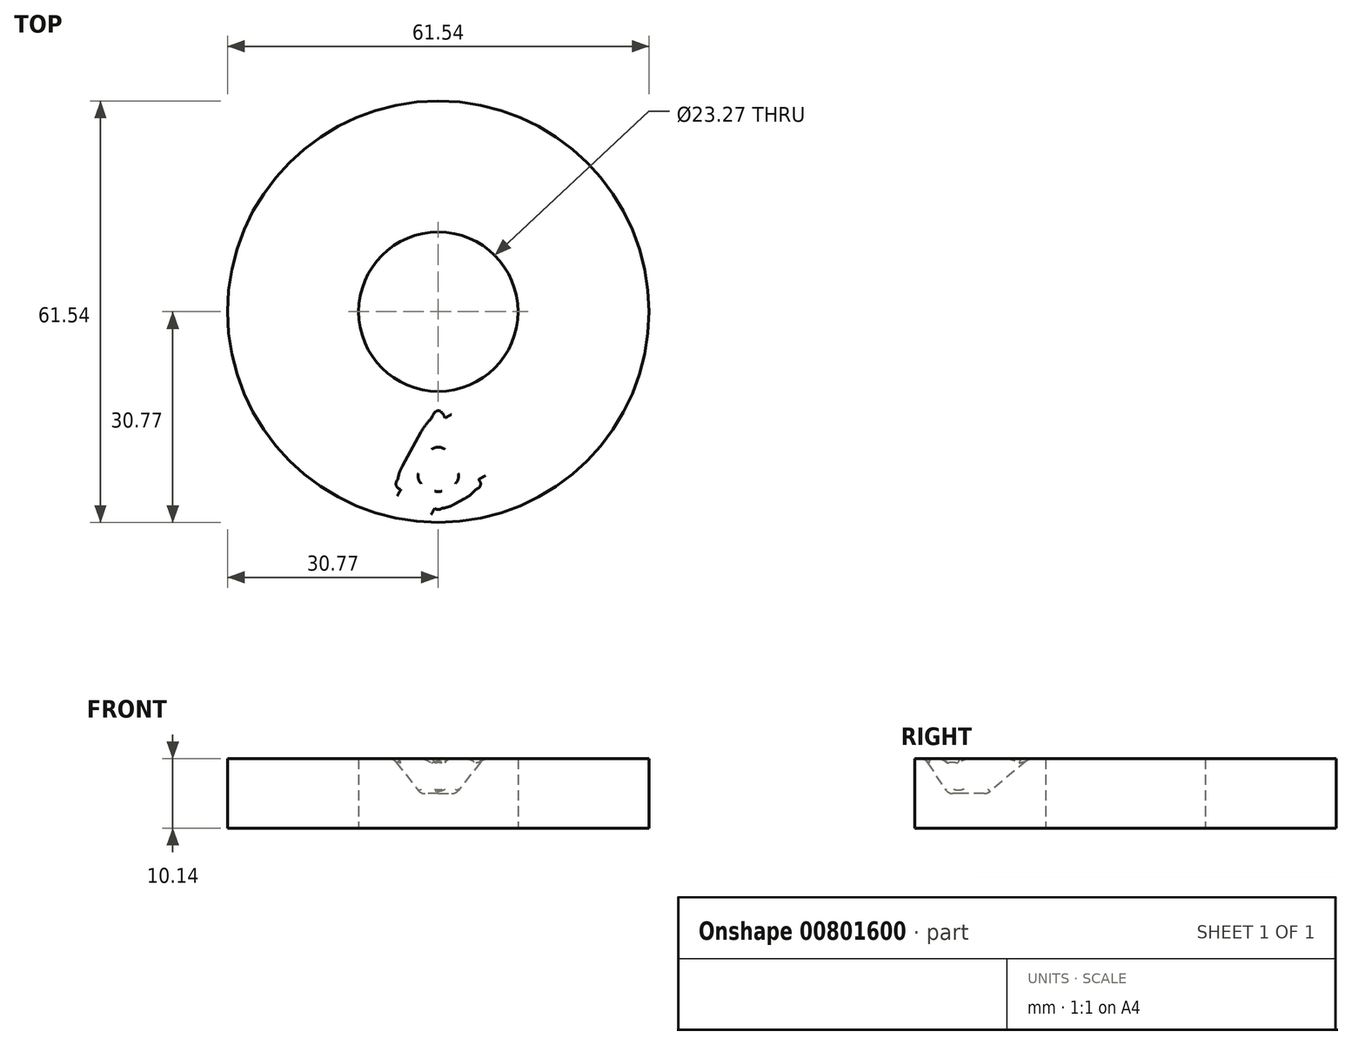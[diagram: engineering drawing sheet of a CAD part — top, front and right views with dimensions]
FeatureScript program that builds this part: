
annotation { "Feature Type Name" : "Feature", "Feature Type Description" : "" }
export const myFeature = defineFeature(function(context is Context, id is Id, definition is map)
    precondition{}
    {
        {
            var Q0;
            Q0=qCreatedBy(makeId("Top.planeOp"),FACE);
            var sketch = newSketch(context, id + "F0", { "sketchPlane" : qUnion([Q0])});
            skCircle(sketch, "E0", {"center": v(0, 0) * mm, "radius": 30.77 * mm});
            skCircle(sketch, "E1", {"center": v(0, 0) * mm, "radius": 11.63 * mm});
            skSolve(sketch);
        }
        {
            var Q0;
            Q0 = qSketchRegion(id + "F0", true);
            extrude(context, id + "F1", {"entities" : qUnion([Q0]), "depth" : 10.14 * mm, "offsetDistance" : 25.4 * mm});
        }
        {
            var Q0;
            Q0=makeQuery(id+"F1.opExtrude","CAP_FACE",FACE,{"disambiguationData":[OSD([sQuery(id+"F0.wireOp",EDGE,"E0"),sQuery(id+"F0.wireOp",EDGE,"E1")])],"isStart":false});
            var sketch = newSketch(context, id + "F2", { "sketchPlane" : qUnion([Q0])});
            skLineSegment(sketch, "E2", {"start": v(24.9, -25.58) * mm, "end": v(0, -13.03) * mm});
            skLineSegment(sketch, "E3", {"start": v(0, -13.03) * mm, "end": v(6.94, -25.58) * mm});
            skLineSegment(sketch, "E4", {"start": v(6.94, -25.58) * mm, "end": v(0, -29.4) * mm});
            skLineSegment(sketch, "E5.MirrorCS", {"start": v(0, -13.03) * mm, "end": v(-6.94, -25.58) * mm});
            skLineSegment(sketch, "E6.MirrorCS", {"start": v(-6.94, -25.58) * mm, "end": v(0, -29.4) * mm});
            skSolve(sketch);
        }
        {
            var Q0;
            Q0=makeQuery(id+"F2.imprint","IMPRINT",FACE,{"disambiguationData":[TD([[makeQuery(id+"F2.imprint","IMPRINT",EDGE,{"derivedFrom":sQuery(id+"F2.wireOp",EDGE,"E3")}),-1.0]])]});
            var Q1;
            Q1 = qSketchRegion(id + "F2", true);
            extrude(context, id + "F3", {"entities" : qUnion([Q0, Q1]), "operationType" : NewBodyOperationType.REMOVE, "oppositeDirection" : true, "depth" : 5.08 * mm, "offsetDistance" : 25.4 * mm, "hasDraft" : true, "draftAngle" : 30 * degree, "draftPullDirection" : true});
        }
        {
            var Q0;
            Q0=makeQuery(id+"F3.boolean.opBoolean","COPY",EDGE,{"derivedFrom":makeQuery(id+"F3.opExtrude","CAP_EDGE",EDGE,{"disambiguationData":[OSD([sQuery(id+"F2.wireOp",EDGE,"E5.MirrorCS")])],"isStart":false})});
            var Q1;
            Q1=makeQuery(id+"F3.boolean.opBoolean","COPY",FACE,{"derivedFrom":makeQuery(id+"F3.opExtrude","CAP_FACE",FACE,{"disambiguationData":[OSD([sQuery(id+"F2.wireOp",EDGE,"E3"),sQuery(id+"F2.wireOp",EDGE,"E4"),sQuery(id+"F2.wireOp",EDGE,"E5.MirrorCS"),sQuery(id+"F2.wireOp",EDGE,"E6.MirrorCS")])],"isStart":false})});
            var Q2;
            Q2=makeQuery(id+"F3.boolean.opBoolean","COPY",EDGE,{"derivedFrom":makeQuery(id+"F3.opExtrude","CAP_EDGE",EDGE,{"disambiguationData":[OSD([sQuery(id+"F2.wireOp",EDGE,"E4")])],"isStart":false})});
            var Q3;
            Q3=makeQuery(id+"F3.boolean.opBoolean","COPY",FACE,{"derivedFrom":makeQuery(id+"F3.opExtrude","SWEPT_FACE",FACE,{"disambiguationData":[OSD([sQuery(id+"F2.wireOp",EDGE,"E6.MirrorCS")])]})});
            var Q4;
            Q4=makeQuery(id+"F3.boolean.opBoolean","COPY",FACE,{"derivedFrom":makeQuery(id+"F3.opExtrude","SWEPT_FACE",FACE,{"disambiguationData":[OSD([sQuery(id+"F2.wireOp",EDGE,"E3")])]})});
            fillet(context, id + "F4", {"entities" : qUnion([Q0, Q1, Q2, Q3, Q4]), "radius" : 1.27 * mm, "tangentPropagation" : true, "allowEdgeOverflow" : false});
        }
    });
